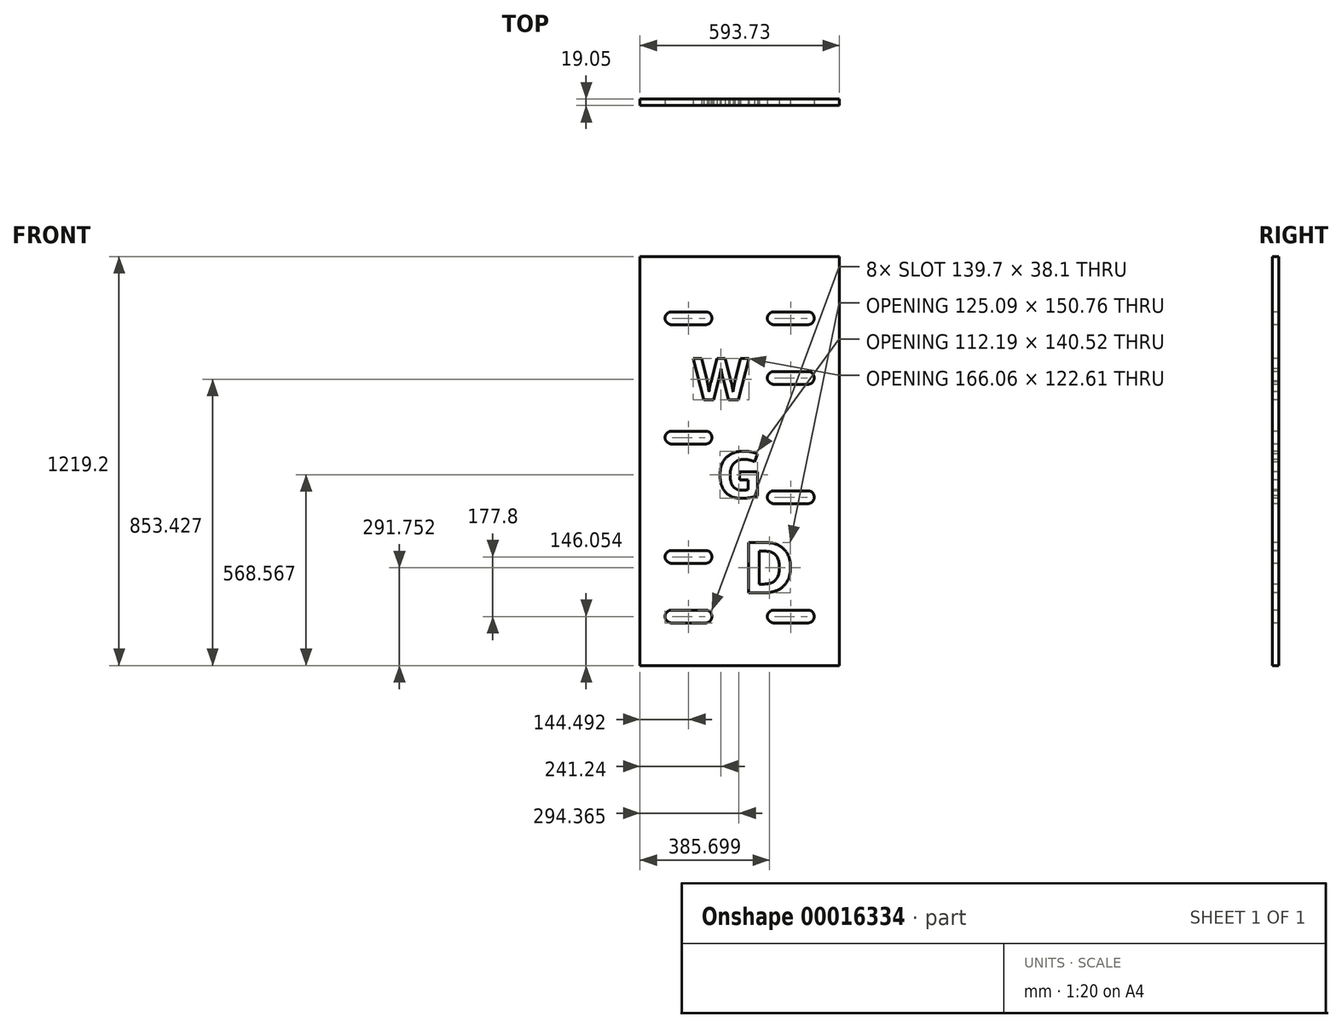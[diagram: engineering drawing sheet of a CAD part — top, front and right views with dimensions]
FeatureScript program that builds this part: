
annotation { "Feature Type Name" : "Feature", "Feature Type Description" : "" }
export const myFeature = defineFeature(function(context is Context, id is Id, definition is map)
    precondition{}
    {
        {
            var Q0;
            Q0=qCreatedBy(makeId("Front.planeOp"),FACE);
            var sketch = newSketch(context, id + "F0", { "sketchPlane" : qUnion([Q0])});
            skLineSegment(sketch, "E0.bottom", {"start": v(0, 29.1) * mm, "end": v(593.72, 29.1) * mm});
            skLineSegment(sketch, "E0.top", {"start": v(0, 1248.3) * mm, "end": v(593.72, 1248.3) * mm});
            skLineSegment(sketch, "E0.left", {"start": v(0, 29.1) * mm, "end": v(0, 1248.3) * mm});
            skLineSegment(sketch, "E0.right", {"start": v(593.73, 29.1) * mm, "end": v(593.73, 1248.3) * mm});
            skSolve(sketch);
        }
        {
            var Q0;
            Q0 = qSketchRegion(id + "F0", true);
            extrude(context, id + "F1", {"entities" : qUnion([Q0]), "depth" : 19.05 * mm});
        }
        {
            var Q0;
            Q0=makeQuery(id+"F1.opExtrude","CAP_FACE",FACE,{"disambiguationData":[OSD([sQuery(id+"F0.wireOp",EDGE,"E0.bottom"),sQuery(id+"F0.wireOp",EDGE,"E0.top"),sQuery(id+"F0.wireOp",EDGE,"E0.left"),sQuery(id+"F0.wireOp",EDGE,"E0.right")])],"isStart":false});
            var sketch = newSketch(context, id + "F2", { "sketchPlane" : qUnion([Q0])});
            skLineSegment(sketch, "E1.bottom", {"start": v(93.7, 156.1) * mm, "end": v(195.3, 156.1) * mm});
            skLineSegment(sketch, "E1.top", {"start": v(93.7, 194.2) * mm, "end": v(195.3, 194.2) * mm});
            skArc(sketch, "E2", {"start": v(195.3, 156.1) * mm, "mid": v(214.34, 175.14) * mm, "end": v(195.3, 194.2) * mm});
            skArc(sketch, "E3", {"start": v(93.7, 194.2) * mm, "mid": v(74.64, 175.14) * mm, "end": v(93.7, 156.1) * mm});
            skArc(sketch, "E4.0.1.0", {"start": v(93.7, 372) * mm, "mid": v(74.64, 352.94) * mm, "end": v(93.7, 333.9) * mm});
            skLineSegment(sketch, "E4.0.1.1", {"start": v(93.7, 333.9) * mm, "end": v(195.3, 333.9) * mm});
            skLineSegment(sketch, "E4.0.1.2", {"start": v(93.7, 372) * mm, "end": v(195.3, 372) * mm});
            skArc(sketch, "E4.0.1.3", {"start": v(195.3, 333.9) * mm, "mid": v(214.34, 352.94) * mm, "end": v(195.3, 372) * mm});
            skArc(sketch, "E4.0.3.0", {"start": v(93.7, 727.6) * mm, "mid": v(74.64, 708.54) * mm, "end": v(93.7, 689.5) * mm});
            skLineSegment(sketch, "E4.0.3.1", {"start": v(93.7, 689.5) * mm, "end": v(195.3, 689.5) * mm});
            skLineSegment(sketch, "E4.0.3.2", {"start": v(93.7, 727.6) * mm, "end": v(195.3, 727.6) * mm});
            skArc(sketch, "E4.0.3.3", {"start": v(195.3, 689.5) * mm, "mid": v(214.34, 708.54) * mm, "end": v(195.3, 727.6) * mm});
            skArc(sketch, "E4.0.5.0", {"start": v(93.7, 1083.2) * mm, "mid": v(74.64, 1064.14) * mm, "end": v(93.7, 1045.1) * mm});
            skLineSegment(sketch, "E4.0.5.1", {"start": v(93.7, 1045.1) * mm, "end": v(195.3, 1045.1) * mm});
            skLineSegment(sketch, "E4.0.5.2", {"start": v(93.7, 1083.2) * mm, "end": v(195.3, 1083.2) * mm});
            skArc(sketch, "E4.0.5.3", {"start": v(195.3, 1045.1) * mm, "mid": v(214.34, 1064.14) * mm, "end": v(195.3, 1083.2) * mm});
            skArc(sketch, "E4.1.0.0", {"start": v(398.5, 194.2) * mm, "mid": v(379.44, 175.14) * mm, "end": v(398.5, 156.1) * mm});
            skLineSegment(sketch, "E4.1.0.1", {"start": v(398.5, 156.1) * mm, "end": v(500.1, 156.1) * mm});
            skLineSegment(sketch, "E4.1.0.2", {"start": v(398.5, 194.2) * mm, "end": v(500.1, 194.2) * mm});
            skArc(sketch, "E4.1.0.3", {"start": v(500.1, 156.1) * mm, "mid": v(519.14, 175.14) * mm, "end": v(500.1, 194.2) * mm});
            skArc(sketch, "E4.1.2.0", {"start": v(398.5, 549.8) * mm, "mid": v(379.44, 530.74) * mm, "end": v(398.5, 511.7) * mm});
            skLineSegment(sketch, "E4.1.2.1", {"start": v(398.5, 511.7) * mm, "end": v(500.1, 511.7) * mm});
            skLineSegment(sketch, "E4.1.2.2", {"start": v(398.5, 549.8) * mm, "end": v(500.1, 549.8) * mm});
            skArc(sketch, "E4.1.2.3", {"start": v(500.1, 511.7) * mm, "mid": v(519.14, 530.74) * mm, "end": v(500.1, 549.8) * mm});
            skArc(sketch, "E4.1.4.0", {"start": v(398.5, 905.4) * mm, "mid": v(379.44, 886.34) * mm, "end": v(398.5, 867.3) * mm});
            skLineSegment(sketch, "E4.1.4.1", {"start": v(398.5, 867.3) * mm, "end": v(500.1, 867.3) * mm});
            skLineSegment(sketch, "E4.1.4.2", {"start": v(398.5, 905.4) * mm, "end": v(500.1, 905.4) * mm});
            skArc(sketch, "E4.1.4.3", {"start": v(500.1, 867.3) * mm, "mid": v(519.14, 886.34) * mm, "end": v(500.1, 905.4) * mm});
            skArc(sketch, "E4.1.5.0", {"start": v(398.5, 1083.2) * mm, "mid": v(379.44, 1064.14) * mm, "end": v(398.5, 1045.1) * mm});
            skLineSegment(sketch, "E4.1.5.1", {"start": v(398.5, 1045.1) * mm, "end": v(500.1, 1045.1) * mm});
            skLineSegment(sketch, "E4.1.5.2", {"start": v(398.5, 1083.2) * mm, "end": v(500.1, 1083.2) * mm});
            skArc(sketch, "E4.1.5.3", {"start": v(500.1, 1045.1) * mm, "mid": v(519.14, 1064.14) * mm, "end": v(500.1, 1083.2) * mm});
            skLineSegment(sketch, "E4.direction1", {"start": v(93.7, 156.1) * mm, "end": v(398.5, 156.1) * mm, "construction": true});
            skLineSegment(sketch, "E4.direction2", {"start": v(93.7, 156.1) * mm, "end": v(93.7, 333.9) * mm, "construction": true});
            skSolve(sketch);
        }
        {
            var Q0;
            Q0 = qSketchRegion(id + "F2", true);
            extrude(context, id + "F3", {"entities" : qUnion([Q0]), "operationType" : NewBodyOperationType.REMOVE, "endBound" : BoundingType.THROUGH_ALL, "oppositeDirection" : true, "depth" : 25.4 * mm});
        }
        {
            var Q0;
            Q0=makeQuery(id+"F1.opExtrude","CAP_FACE",FACE,{"disambiguationData":[OSD([sQuery(id+"F0.wireOp",EDGE,"E0.bottom"),sQuery(id+"F0.wireOp",EDGE,"E0.top"),sQuery(id+"F0.wireOp",EDGE,"E0.left"),sQuery(id+"F0.wireOp",EDGE,"E0.right")])],"isStart":false});
            var sketch = newSketch(context, id + "F4", { "sketchPlane" : qUnion([Q0])});
            skText(sketch, "E5", { "text": "W", "fontName": "OpenSans-Bold.ttf"});
            skText(sketch, "E6", { "text": "W", "fontName": "OpenSans-Bold.ttf"});
            skText(sketch, "E7", { "text": "G", "fontName": "OpenSans-Bold.ttf"});
            skText(sketch, "E8", { "text": "D", "fontName": "OpenSans-Bold.ttf"});
            const initialGuessF4  = {"E5": [0.15821, 0.82121, 1, 0, 0.12366], "E6": [0.41981, 1.56944, 1, 0, 0.12366], "E7": [0.22714, 0.52928, 1, 0, 0.13786], "E8": [0.30418, 0.24546, 1, 0, 0.15205]};
            skSetInitialGuess(sketch, initialGuessF4);
            skSolve(sketch);
        }
        {
            var Q0;
            Q0 = qSketchRegion(id + "F4", true);
            extrude(context, id + "F5", {"entities" : qUnion([Q0]), "operationType" : NewBodyOperationType.REMOVE, "endBound" : BoundingType.THROUGH_ALL, "oppositeDirection" : true, "depth" : 25.4 * mm});
        }
    });
